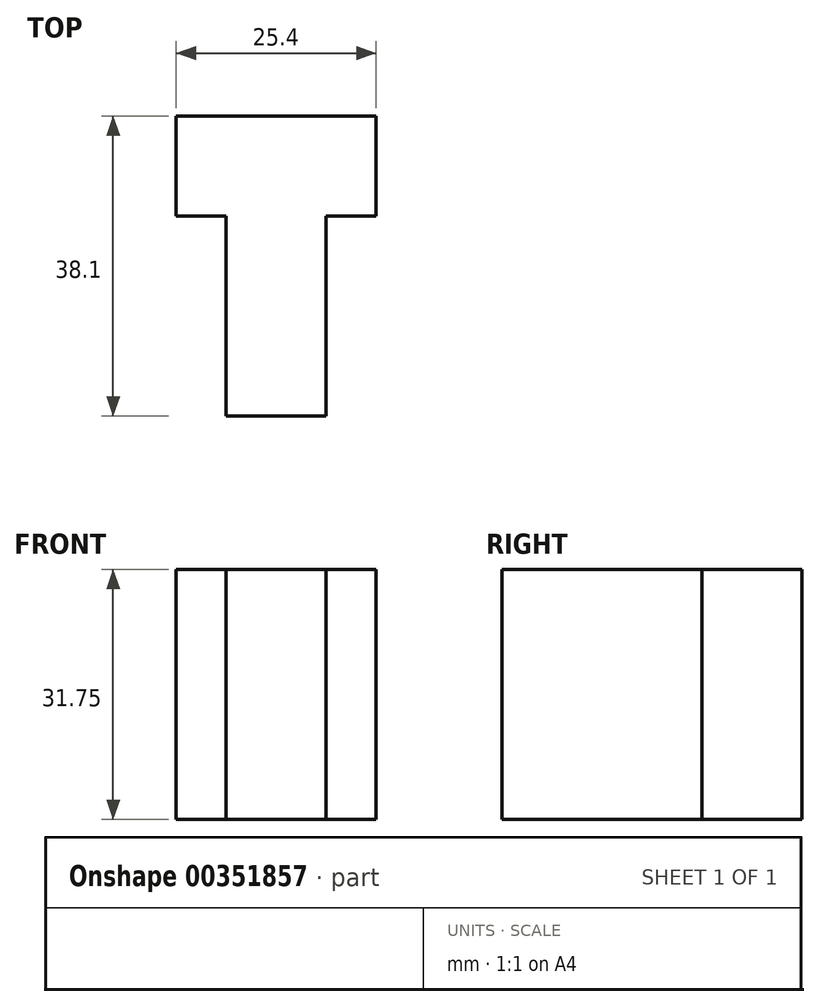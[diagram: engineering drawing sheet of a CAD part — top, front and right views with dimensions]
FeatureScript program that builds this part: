
annotation { "Feature Type Name" : "Feature", "Feature Type Description" : "" }
export const myFeature = defineFeature(function(context is Context, id is Id, definition is map)
    precondition{}
    {
        {
            var Q0;
            Q0=qCreatedBy(makeId("Top.planeOp"),FACE);
            var sketch = newSketch(context, id + "F0", { "sketchPlane" : qUnion([Q0])});
            skLineSegment(sketch, "E0", {"start": v(0, 0) * mm, "end": v(12.7, 0) * mm});
            skLineSegment(sketch, "E1", {"start": v(12.7, 0) * mm, "end": v(12.7, 25.4) * mm});
            skLineSegment(sketch, "E2", {"start": v(12.7, 25.4) * mm, "end": v(19.05, 25.4) * mm});
            skLineSegment(sketch, "E3", {"start": v(19.05, 25.4) * mm, "end": v(19.05, 38.1) * mm});
            skLineSegment(sketch, "E4", {"start": v(19.05, 38.1) * mm, "end": v(-6.35, 38.1) * mm});
            skLineSegment(sketch, "E5", {"start": v(-6.35, 38.1) * mm, "end": v(-6.35, 25.4) * mm});
            skLineSegment(sketch, "E6", {"start": v(-6.35, 25.4) * mm, "end": v(0, 25.4) * mm});
            skLineSegment(sketch, "E7", {"start": v(0, 25.4) * mm, "end": v(0, 0) * mm});
            skSolve(sketch);
        }
        {
            var Q0;
            Q0 = qSketchRegion(id + "F0", true);
            extrude(context, id + "F1", {"entities" : qUnion([Q0]), "depth" : 31.75 * mm});
        }
    });
